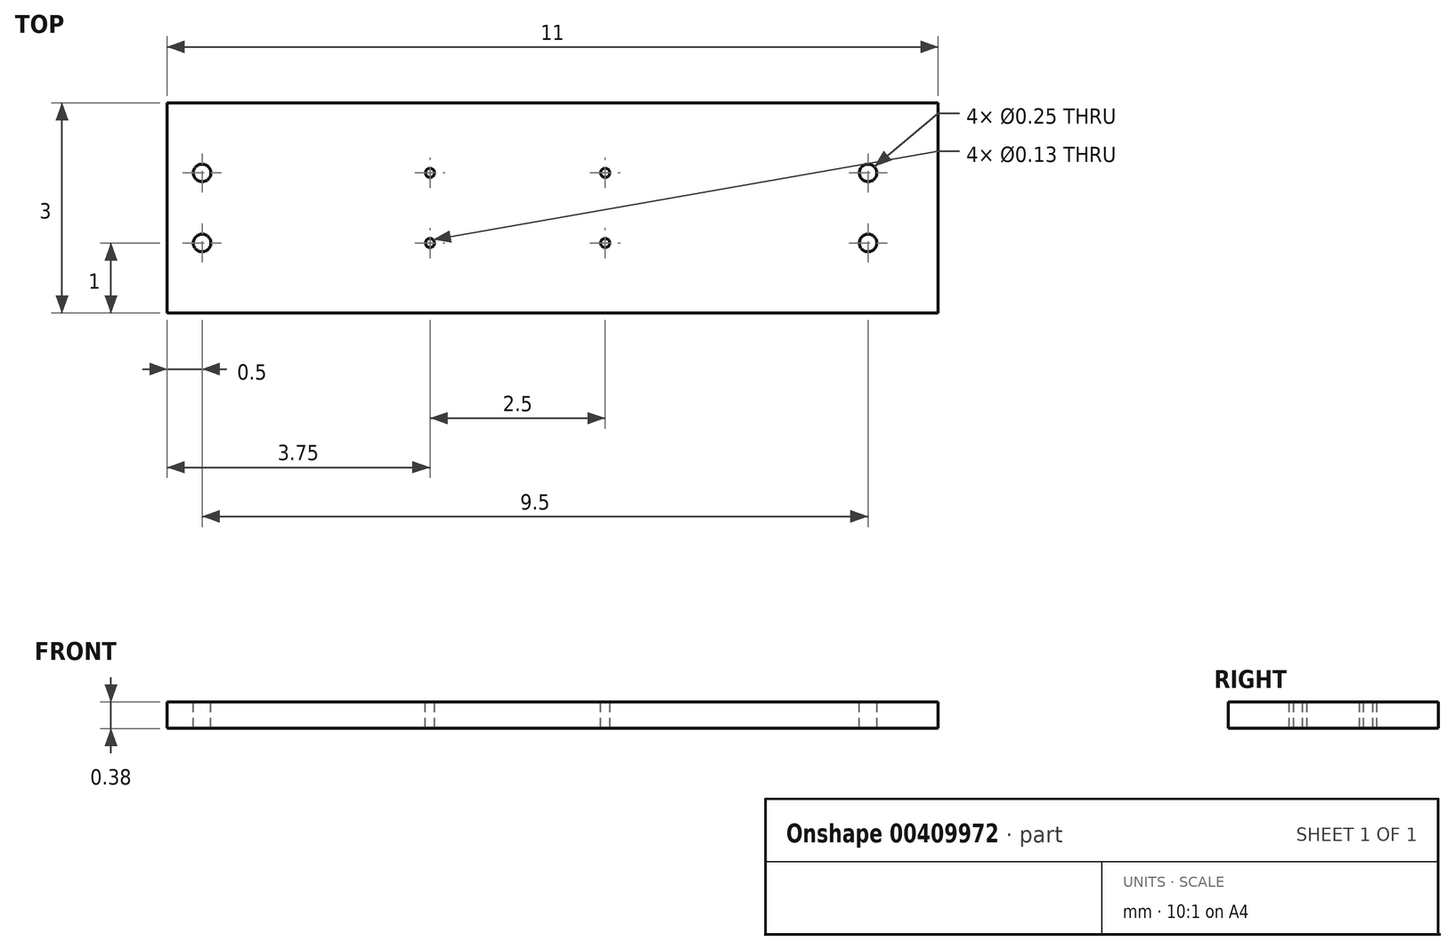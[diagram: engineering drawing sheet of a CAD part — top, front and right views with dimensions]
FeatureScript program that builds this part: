
annotation { "Feature Type Name" : "Feature", "Feature Type Description" : "" }
export const myFeature = defineFeature(function(context is Context, id is Id, definition is map)
    precondition{}
    {
        {
            var Q0;
            Q0=qCreatedBy(makeId("Top.planeOp"),FACE);
            var sketch = newSketch(context, id + "F0", { "sketchPlane" : qUnion([Q0])});
            skLineSegment(sketch, "E0.bottom", {"start": v(0, 0) * mm, "end": v(11, 0) * mm});
            skLineSegment(sketch, "E0.top", {"start": v(0, 3) * mm, "end": v(11, 3) * mm});
            skLineSegment(sketch, "E0.left", {"start": v(0, 0) * mm, "end": v(0, 3) * mm});
            skLineSegment(sketch, "E0.right", {"start": v(11, 0) * mm, "end": v(11, 3) * mm});
            skSolve(sketch);
        }
        {
            var Q0;
            Q0=makeQuery(id+"F0.imprint","IMPRINT",FACE,{"disambiguationData":[TD([[makeQuery(id+"F0.imprint","IMPRINT",EDGE,{"derivedFrom":sQuery(id+"F0.wireOp",EDGE,"E0.bottom")}),1.0]])]});
            extrude(context, id + "F1", {"entities" : qUnion([Q0]), "oppositeDirection" : true, "depth" : 0.38 * mm});
        }
        {
            var Q0;
            Q0=makeQuery(id+"F1.opExtrude","CAP_FACE",FACE,{"disambiguationData":[OSD([sQuery(id+"F0.wireOp",EDGE,"E0.bottom"),sQuery(id+"F0.wireOp",EDGE,"E0.top"),sQuery(id+"F0.wireOp",EDGE,"E0.left"),sQuery(id+"F0.wireOp",EDGE,"E0.right")])],"isStart":true});
            var sketch = newSketch(context, id + "F2", { "sketchPlane" : qUnion([Q0])});
            skCircle(sketch, "E1", {"center": v(10, 2) * mm, "radius": 0.12 * mm});
            skCircle(sketch, "E2", {"center": v(10, 1) * mm, "radius": 0.12 * mm});
            skCircle(sketch, "E3", {"center": v(6.25, 2) * mm, "radius": 0.07 * mm});
            skCircle(sketch, "E4", {"center": v(6.25, 1) * mm, "radius": 0.07 * mm});
            skCircle(sketch, "E5", {"center": v(3.75, 2) * mm, "radius": 0.07 * mm});
            skCircle(sketch, "E6", {"center": v(3.75, 1) * mm, "radius": 0.06 * mm});
            skCircle(sketch, "E7", {"center": v(0.5, 2) * mm, "radius": 0.12 * mm});
            skCircle(sketch, "E8", {"center": v(0.5, 1) * mm, "radius": 0.12 * mm});
            skSolve(sketch);
        }
        {
            var Q0;
            Q0=makeQuery(id+"F2.imprint","IMPRINT",FACE,{"disambiguationData":[TD([[makeQuery(id+"F2.imprint","IMPRINT",EDGE,{"derivedFrom":sQuery(id+"F2.wireOp",EDGE,"E2")}),1.0]])]});
            var Q1;
            Q1=makeQuery(id+"F2.imprint","IMPRINT",FACE,{"disambiguationData":[TD([[makeQuery(id+"F2.imprint","IMPRINT",EDGE,{"derivedFrom":sQuery(id+"F2.wireOp",EDGE,"E1")}),1.0]])]});
            var Q2;
            Q2=makeQuery(id+"F2.imprint","IMPRINT",FACE,{"disambiguationData":[TD([[makeQuery(id+"F2.imprint","IMPRINT",EDGE,{"derivedFrom":sQuery(id+"F2.wireOp",EDGE,"E3")}),1.0]])]});
            var Q3;
            Q3=makeQuery(id+"F2.imprint","IMPRINT",FACE,{"disambiguationData":[TD([[makeQuery(id+"F2.imprint","IMPRINT",EDGE,{"derivedFrom":sQuery(id+"F2.wireOp",EDGE,"E4")}),1.0]])]});
            var Q4;
            Q4=makeQuery(id+"F2.imprint","IMPRINT",FACE,{"disambiguationData":[TD([[makeQuery(id+"F2.imprint","IMPRINT",EDGE,{"derivedFrom":sQuery(id+"F2.wireOp",EDGE,"E5")}),1.0]])]});
            var Q5;
            Q5=makeQuery(id+"F2.imprint","IMPRINT",FACE,{"disambiguationData":[TD([[makeQuery(id+"F2.imprint","IMPRINT",EDGE,{"derivedFrom":sQuery(id+"F2.wireOp",EDGE,"E6")}),1.0]])]});
            var Q6;
            Q6=makeQuery(id+"F2.imprint","IMPRINT",FACE,{"disambiguationData":[TD([[makeQuery(id+"F2.imprint","IMPRINT",EDGE,{"derivedFrom":sQuery(id+"F2.wireOp",EDGE,"E7")}),1.0]])]});
            var Q7;
            Q7=makeQuery(id+"F2.imprint","IMPRINT",FACE,{"disambiguationData":[TD([[makeQuery(id+"F2.imprint","IMPRINT",EDGE,{"derivedFrom":sQuery(id+"F2.wireOp",EDGE,"E8")}),1.0]])]});
            extrude(context, id + "F3", {"entities" : qUnion([Q0, Q1, Q2, Q3, Q4, Q5, Q6, Q7]), "operationType" : NewBodyOperationType.REMOVE, "endBound" : BoundingType.THROUGH_ALL, "oppositeDirection" : true, "depth" : 25 * mm});
        }
    });
